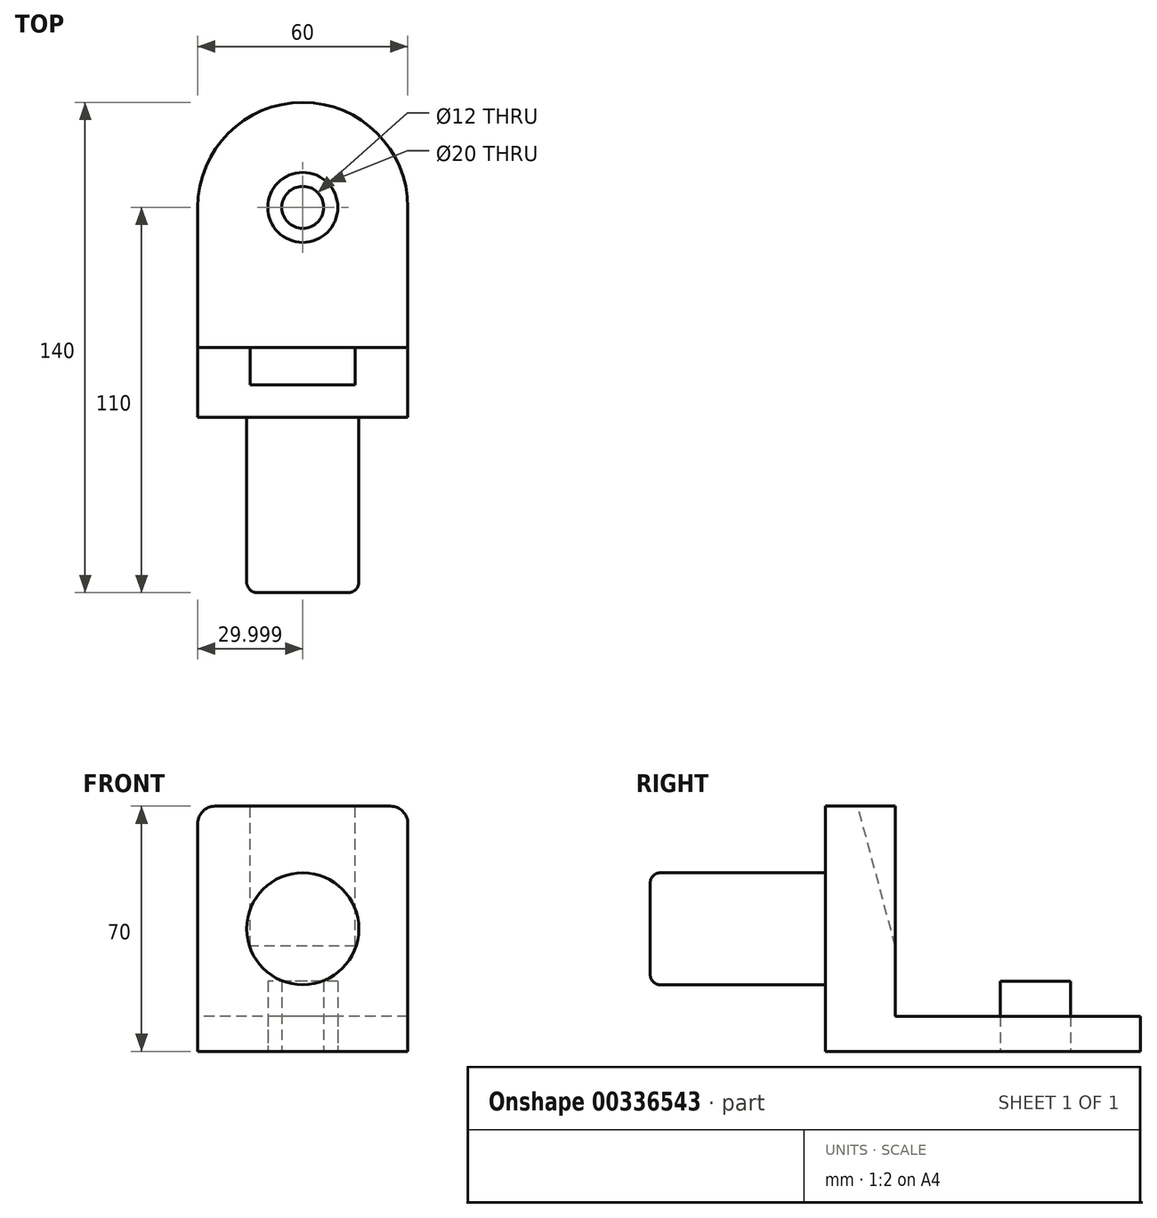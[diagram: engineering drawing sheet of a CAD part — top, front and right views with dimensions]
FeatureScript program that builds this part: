
annotation { "Feature Type Name" : "Feature", "Feature Type Description" : "" }
export const myFeature = defineFeature(function(context is Context, id is Id, definition is map)
    precondition{}
    {
        {
            var Q0;
            Q0=qCreatedBy(makeId("Top.planeOp"),FACE);
            var sketch = newSketch(context, id + "F0", { "sketchPlane" : qUnion([Q0])});
            skLineSegment(sketch, "E0", {"start": v(-21.66, -50) * mm, "end": v(-21.66, 0) * mm});
            skLineSegment(sketch, "E1", {"start": v(-21.66, 0) * mm, "end": v(10.34, 0) * mm});
            skLineSegment(sketch, "E2", {"start": v(10.34, 0) * mm, "end": v(10.34, -50) * mm});
            skLineSegment(sketch, "E3", {"start": v(10.34, -50) * mm, "end": v(-21.66, -50) * mm});
            skLineSegment(sketch, "E4", {"start": v(-21.66, 0) * mm, "end": v(-35.66, 0) * mm});
            skLineSegment(sketch, "E5", {"start": v(10.34, 0) * mm, "end": v(24.34, 0) * mm});
            skLineSegment(sketch, "E6", {"start": v(24.34, 0) * mm, "end": v(24.34, 60) * mm});
            skLineSegment(sketch, "E7", {"start": v(-5.66, 90) * mm, "end": v(-5.66, 90) * mm});
            skLineSegment(sketch, "E8", {"start": v(-35.66, 0) * mm, "end": v(-35.66, 60) * mm});
            skLineSegment(sketch, "E9", {"start": v(24.34, 20) * mm, "end": v(-35.66, 20) * mm});
            skPoint(sketch, "E10.end.orphan", {"position": v(-21.66, 20) * mm});
            skPoint(sketch, "E11.visualSharp", {"position": v(24.34, 90) * mm});
            skArc(sketch, "E11.filletArc", {"start": v(24.34, 60) * mm, "mid": v(15.55, 81.21) * mm, "end": v(-5.66, 90) * mm});
            skPoint(sketch, "E12.visualSharp", {"position": v(-35.66, 90) * mm});
            skArc(sketch, "E12.filletArc", {"start": v(-5.66, 90) * mm, "mid": v(-26.87, 81.21) * mm, "end": v(-35.66, 60) * mm});
            skCircle(sketch, "E13", {"center": v(-5.66, 60) * mm, "radius": 6 * mm});
            skCircle(sketch, "E14", {"center": v(-5.66, 60) * mm, "radius": 10 * mm});
            skSolve(sketch);
        }
        {
            var Q0;
            {var subQ1=sQuery(id+"F0.wireOp",EDGE,"E9");Q0=makeQuery(id+"F0.imprint","IMPRINT",FACE,{"disambiguationData":[TD([[makeQuery(id+"F0.imprint","IMPRINT",EDGE,{"derivedFrom":subQ1}),-1.0]])]});}
            extrude(context, id + "F1", {"entities" : qUnion([Q0]), "depth" : 10 * mm});
        }
        {
            var Q0;
            Q0=makeQuery(id+"F0.imprint","IMPRINT",FACE,{"disambiguationData":[TD([[makeQuery(id+"F0.imprint","IMPRINT",EDGE,{"derivedFrom":sQuery(id+"F0.wireOp",EDGE,"E13")}),-1.0]])]});
            extrude(context, id + "F2", {"entities" : qUnion([Q0]), "depth" : 20 * mm});
        }
        {
            var Q0;
            Q0=makeQuery(id+"F0.imprint","IMPRINT",FACE,{"disambiguationData":[TD([[makeQuery(id+"F0.imprint","IMPRINT",EDGE,{"derivedFrom":sQuery(id+"F0.wireOp",EDGE,"E1")}),1.0]])]});
            extrude(context, id + "F3", {"entities" : qUnion([Q0]), "operationType" : NewBodyOperationType.ADD, "depth" : 70 * mm});
        }
        {
            var Q0;
            {var subQ0=sQuery(id+"F0.wireOp",EDGE,"E8");Q0=makeQuery(id+"F3.boolean.opBoolean","MERGE",FACE,{"derivedFrom":[makeQuery(id+"F1.opExtrude","SWEPT_FACE",FACE,{"disambiguationData":[OSD([subQ0])]}),makeQuery(id+"F3.opExtrude","SWEPT_FACE",FACE,{"disambiguationData":[OSD([subQ0])]})]});}
            var sketch = newSketch(context, id + "F4", { "sketchPlane" : qUnion([Q0])});
            skLineSegment(sketch, "E15", {"start": v(-20, 70) * mm, "end": v(-20, 30) * mm});
            skPoint(sketch, "E16.end.orphan", {"position": v(-20, 40) * mm});
            skPoint(sketch, "E17.orphan", {"position": v(-10, 70) * mm});
            skLineSegment(sketch, "E18", {"start": v(-20, 30) * mm, "end": v(-9.28, 70) * mm});
            skLineSegment(sketch, "E19", {"start": v(-9.28, 70) * mm, "end": v(-20, 70) * mm});
            skSolve(sketch);
        }
        {
            var Q0;
            {var subQ0=sQuery(id+"F4.wireOp",EDGE,"E15");Q0=makeQuery(id+"F4.imprint","IMPRINT",FACE,{"disambiguationData":[TD([[makeQuery(id+"F4.imprint","IMPRINT",EDGE,{"derivedFrom":subQ0}),1.0]])]});}
            extrude(context, id + "F5", {"entities" : qUnion([Q0]), "operationType" : NewBodyOperationType.REMOVE, "oppositeDirection" : true, "depth" : 60 * mm});
        }
        {
            var Q0;
            {var subQ3=sQuery(id+"F4.wireOp",EDGE,"kkNFssZg-NDKe-HPsH-PYxm-5HKryJ16R8jP");Q0=makeQuery(id+"F4.imprint","IMPRINT",FACE,{"disambiguationData":[TD([[makeQuery(id+"F4.imprint","IMPRINT",EDGE,{"derivedFrom":subQ3}),-1.0]])]});}
            var Q1;
            {var subQ0=sQuery(id+"F4.wireOp",EDGE,"E15");Q1=makeQuery(id+"F4.imprint","IMPRINT",FACE,{"disambiguationData":[TD([[makeQuery(id+"F4.imprint","IMPRINT",EDGE,{"derivedFrom":subQ0}),1.0]])]});}
            extrude(context, id + "F6", {"entities" : qUnion([Q0, Q1]), "operationType" : NewBodyOperationType.ADD, "oppositeDirection" : true, "depth" : 15 * mm});
        }
        {
            var Q0;
            {var subQ0=sQuery(id+"F0.wireOp",EDGE,"E6");Q0=makeQuery(id+"F3.boolean.opBoolean","MERGE",FACE,{"derivedFrom":[makeQuery(id+"F1.opExtrude","SWEPT_FACE",FACE,{"disambiguationData":[OSD([subQ0])]}),makeQuery(id+"F3.opExtrude","SWEPT_FACE",FACE,{"disambiguationData":[OSD([subQ0])]})]});}
            var sketch = newSketch(context, id + "F7", { "sketchPlane" : qUnion([Q0])});
            skLineSegment(sketch, "E20", {"start": v(9.28, 70) * mm, "end": v(20, 30) * mm});
            skLineSegment(sketch, "E21", {"start": v(20, 30) * mm, "end": v(20, 70) * mm});
            skLineSegment(sketch, "E22", {"start": v(20, 70) * mm, "end": v(9.28, 70) * mm});
            skSolve(sketch);
        }
        {
            var Q0;
            {var subQ0=sQuery(id+"F0.wireOp",EDGE,"E8");var subQ1=makeQuery(id+"F3.opExtrude","CAP_EDGE",EDGE,{"disambiguationData":[OSD([subQ0])],"isStart":false});var subQ2=makeQuery(id+"F4.imprint","INTERSECT",VERTEX,{"derivedFrom":[subQ1,sQuery(id+"F4.wireOp",EDGE,"kkNFssZg-NDKe-HPsH-PYxm-5HKryJ16R8jP")]});Q0=makeQuery(id+"F6.boolean.opBoolean","MERGE",EDGE,{"derivedFrom":[subQ1,makeQuery(id+"F6.opExtrude","CAP_EDGE",EDGE,{"disambiguationData":[OSD([subQ0]),TDD([makeQuery(id+"F4.imprint","IMPRINT",EDGE,{"disambiguationData":[TD([[subQ2,1.0]])],"derivedFrom":subQ1}),makeQuery(id+"F4.imprint","IMPRINT",EDGE,{"disambiguationData":[TD([[makeQuery(id+"F4.imprint","INTERSECT",VERTEX,{"derivedFrom":[subQ1,sQuery(id+"F4.wireOp",EDGE,"E15")]}),1.0]])],"derivedFrom":subQ1})])],"isStart":true})]});}
            fillet(context, id + "F8", {"entities" : qUnion([Q0]), "radius" : 5 * mm, "tangentPropagation" : true, "allowEdgeOverflow" : false});
        }
        {
            var Q0;
            Q0=makeQuery(id+"F7.imprint","IMPRINT",FACE,{"disambiguationData":[TD([[makeQuery(id+"F7.imprint","IMPRINT",EDGE,{"derivedFrom":sQuery(id+"F7.wireOp",EDGE,"E20")}),-1.0]])]});
            extrude(context, id + "F9", {"entities" : qUnion([Q0]), "operationType" : NewBodyOperationType.ADD, "oppositeDirection" : true, "depth" : 15 * mm});
        }
        {
            var Q0;
            Q0=makeQuery(id+"F9.boolean.opBoolean","MERGE",EDGE,{"derivedFrom":[makeQuery(id+"F3.opExtrude","CAP_EDGE",EDGE,{"disambiguationData":[OSD([sQuery(id+"F0.wireOp",EDGE,"E6")])],"isStart":false}),makeQuery(id+"F9.opExtrude","CAP_EDGE",EDGE,{"disambiguationData":[OSD([sQuery(id+"F7.wireOp",EDGE,"E22")])],"isStart":true})]});
            fillet(context, id + "F10", {"entities" : qUnion([Q0]), "radius" : 5 * mm, "tangentPropagation" : true, "allowEdgeOverflow" : false});
        }
        {
            var Q0;
            Q0=makeQuery(id+"F3.opExtrude","SWEPT_FACE",FACE,{"disambiguationData":[OSD([sQuery(id+"F0.wireOp",EDGE,"E1"),sQuery(id+"F0.wireOp",EDGE,"E4"),sQuery(id+"F0.wireOp",EDGE,"E5")])]});
            var sketch = newSketch(context, id + "F11", { "sketchPlane" : qUnion([Q0])});
            skLineSegment(sketch, "E23", {"start": v(-5.66, 0) * mm, "end": v(-5.66, 19) * mm});
            skLineSegment(sketch, "E24", {"start": v(-5.66, 70) * mm, "end": v(-5.66, 51) * mm});
            skPoint(sketch, "E24.endSnap0", {"position": v(-5.66, 70) * mm});
            skLineSegment(sketch, "E25", {"start": v(-5.66, 51) * mm, "end": v(-5.66, 35) * mm});
            skLineSegment(sketch, "E26", {"start": v(-5.66, 35) * mm, "end": v(-5.66, 19) * mm});
            skCircle(sketch, "E27", {"center": v(-5.66, 35) * mm, "radius": 16 * mm});
            skSolve(sketch);
        }
        {
            var Q0;
            {var subQ0=sQuery(id+"F11.wireOp",EDGE,"E25");Q0=makeQuery(id+"F11.imprint","IMPRINT",FACE,{"disambiguationData":[TD([[makeQuery(id+"F11.imprint","IMPRINT",EDGE,{"derivedFrom":subQ0}),1.0]])]});}
            var Q1;
            {var subQ0=sQuery(id+"F11.wireOp",EDGE,"E25");Q1=makeQuery(id+"F11.imprint","IMPRINT",FACE,{"disambiguationData":[TD([[makeQuery(id+"F11.imprint","IMPRINT",EDGE,{"derivedFrom":subQ0}),-1.0]])]});}
            extrude(context, id + "F12", {"entities" : qUnion([Q0, Q1]), "operationType" : NewBodyOperationType.ADD, "depth" : 50 * mm});
        }
        {
            var Q0;
            Q0=makeQuery(id+"F12.opExtrude","CAP_EDGE",EDGE,{"disambiguationData":[OSD([sQuery(id+"F11.wireOp",EDGE,"E27")])],"isStart":false});
            fillet(context, id + "F13", {"entities" : qUnion([Q0]), "radius" : 3 * mm, "tangentPropagation" : true, "allowEdgeOverflow" : false});
        }
    });
